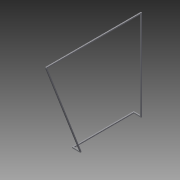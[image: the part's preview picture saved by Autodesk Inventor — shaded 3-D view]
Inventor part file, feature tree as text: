
AUTODESK INVENTOR PART (.ipt)
format: ipt  version: 2013 (Build 170138000, 138)  size: 116,736 bytes
history: native  units: in
note: dims shown in document units (in); Inventor stores cm internally (conversion verified against a paired STEP export)
features: extrude x5, sketch x5
ambient origin geometry x8: Origin, YZ Plane, XZ Plane, XY Plane, X Axis, Y Axis, Z Axis, Center Point
bodies: Solid1 (feature_tree)
feature tree (10):
  extrude  "Extrusion1"  Depth=15.0in
  extrude  "Extrusion2"  Depth=0.25in
  extrude  "Extrusion3"  Depth=0.25in
  extrude  "Extrusion4"  Depth=1.5in TaperAngle=0.0deg
  extrude  "Extrusion5"  Depth=22.0in
  sketch  "Sketch1"  dims[d0=0.25in d1=15.0in]
  sketch  "Sketch2"  dims[d2=0.25in d3=0.0in d4=0.25in]
  sketch  "Sketch3"  dims[d5=0.25in d6=0.25in]
  sketch  "Sketch4"  dims[d7=0.25in d8=1.5in d9=0.0in]
  sketch  "Sketch5"  dims[d10=0.25in d11=22.0in d12=0.25in d13=0.0in d14=23.25in d15=0.25in d16=0.25in d17=0.0in d18=21.75in d20=8.25in d22=0.25in d23=90.0deg d24=0.25in d25=0.25in d26=0.25in d27=0.0in]
